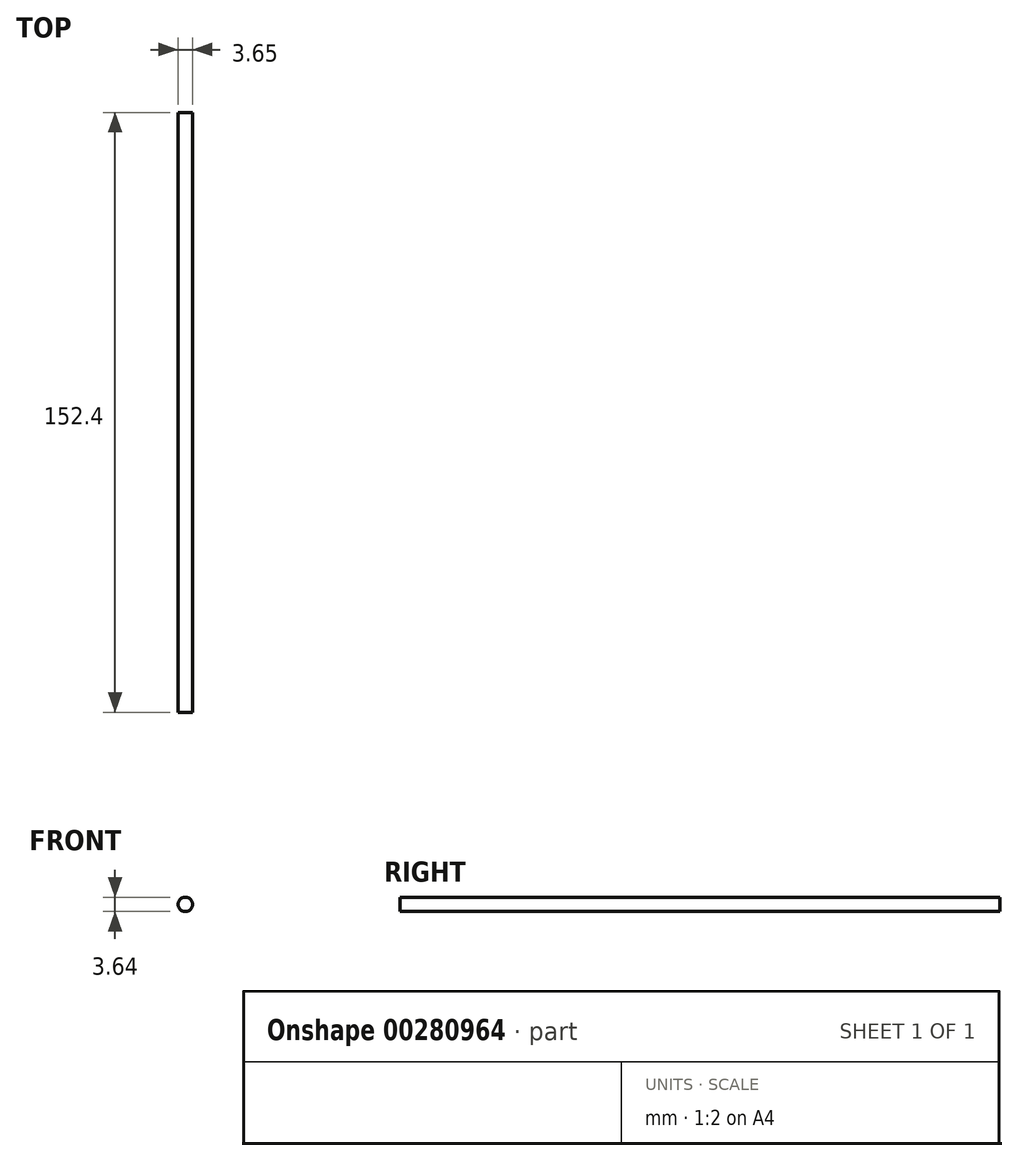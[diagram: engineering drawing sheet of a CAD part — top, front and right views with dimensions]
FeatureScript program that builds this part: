
annotation { "Feature Type Name" : "Feature", "Feature Type Description" : "" }
export const myFeature = defineFeature(function(context is Context, id is Id, definition is map)
    precondition{}
    {
        {
            var Q0;
            Q0=qCreatedBy(makeId("Front.planeOp"),FACE);
            var sketch = newSketch(context, id + "F0", { "sketchPlane" : qUnion([Q0])});
            skCircle(sketch, "E0", {"center": v(-30.36, 25.96) * mm, "radius": 1.82 * mm});
            skSolve(sketch);
        }
        {
            var Q0;
            Q0=makeQuery(id+"F0.imprint","IMPRINT",FACE,{"disambiguationData":[TD([[makeQuery(id+"F0.imprint","IMPRINT",EDGE,{"derivedFrom":sQuery(id+"F0.wireOp",EDGE,"E0")}),1.0]])]});
            extrude(context, id + "F1", {"entities" : qUnion([Q0]), "depth" : 152.4 * mm});
        }
    });
